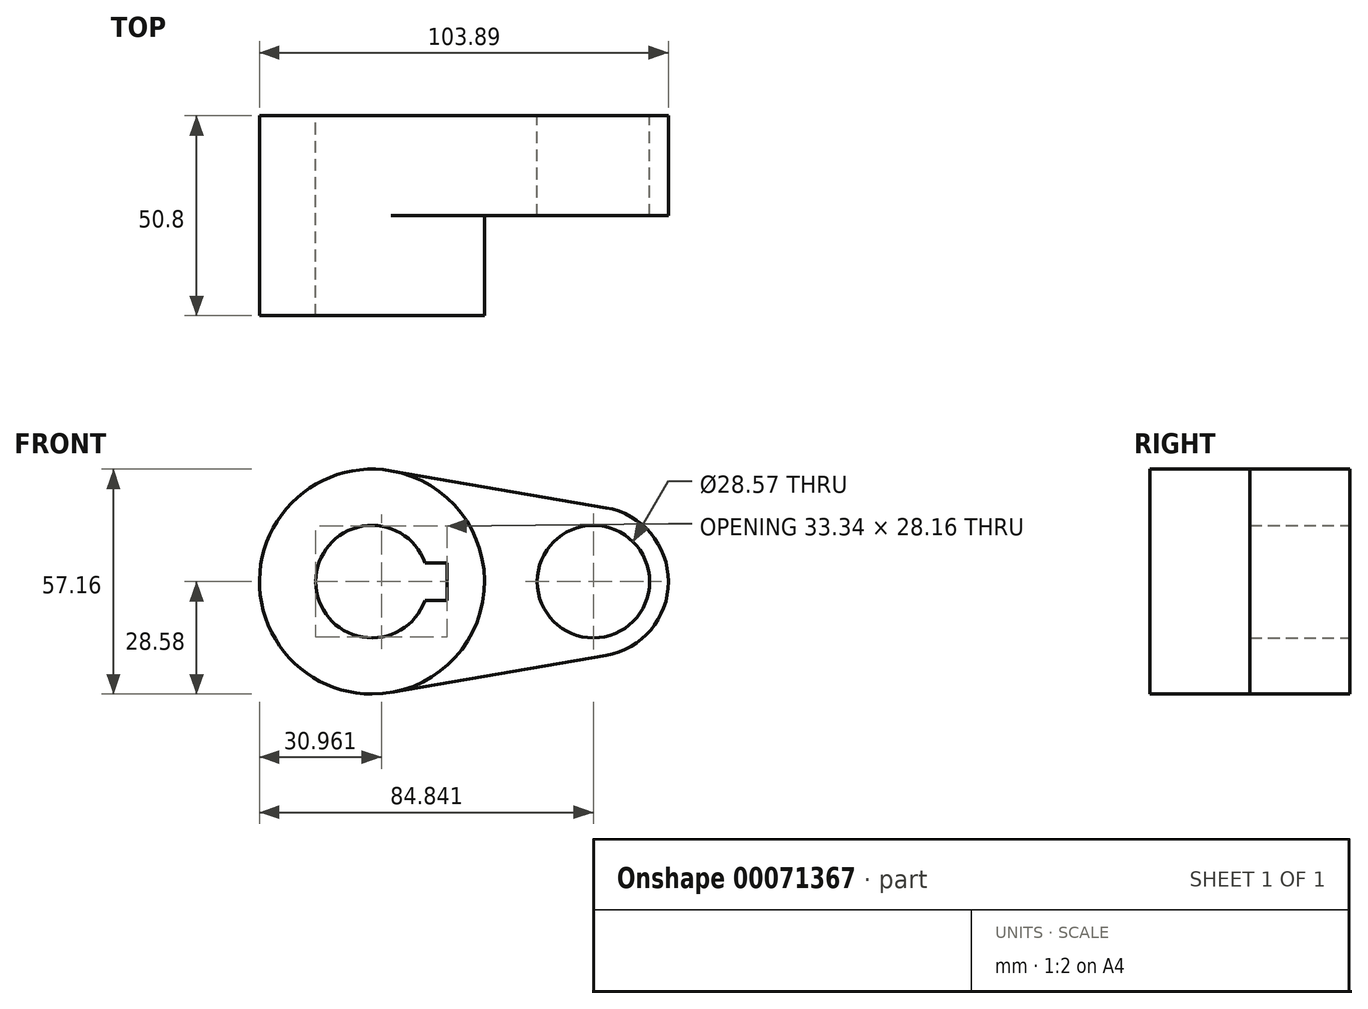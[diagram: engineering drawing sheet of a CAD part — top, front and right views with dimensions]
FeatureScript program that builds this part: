
annotation { "Feature Type Name" : "Feature", "Feature Type Description" : "" }
export const myFeature = defineFeature(function(context is Context, id is Id, definition is map)
    precondition{}
    {
        {
            var Q0;
            Q0=qCreatedBy(makeId("Front.planeOp"),FACE);
            var sketch = newSketch(context, id + "F0", { "sketchPlane" : qUnion([Q0])});
            skCircle(sketch, "E0", {"center": v(0, 0) * mm, "radius": 28.57 * mm});
            skCircle(sketch, "E1", {"center": v(56.26, 0) * mm, "radius": 19.05 * mm});
            skLineSegment(sketch, "E2", {"start": v(4.84, 28.16) * mm, "end": v(59.49, 18.78) * mm});
            skLineSegment(sketch, "E3", {"start": v(4.84, -28.16) * mm, "end": v(59.49, -18.78) * mm});
            skCircle(sketch, "E4", {"center": v(0, 0) * mm, "radius": 14.29 * mm});
            skCircle(sketch, "E5", {"center": v(56.26, 0) * mm, "radius": 14.29 * mm});
            skLineSegment(sketch, "E6.bottom", {"start": v(-19.05, 4.76) * mm, "end": v(19.05, 4.76) * mm});
            skLineSegment(sketch, "E6.top", {"start": v(-19.05, -4.76) * mm, "end": v(19.05, -4.76) * mm});
            skLineSegment(sketch, "E6.left", {"start": v(-19.05, 4.76) * mm, "end": v(-19.05, -4.76) * mm});
            skLineSegment(sketch, "E6.right", {"start": v(19.05, 4.76) * mm, "end": v(19.05, -4.76) * mm});
            skSolve(sketch);
        }
        {
            var Q0;
            {var subQ11=sQuery(id+"F0.wireOp",EDGE,"E6.left");Q0=makeQuery(id+"F0.imprint","IMPRINT",FACE,{"disambiguationData":[TD([[makeQuery(id+"F0.imprint","IMPRINT",EDGE,{"derivedFrom":subQ11}),-1.0]])]});}
            var Q1;
            {var subQ5=sQuery(id+"F0.wireOp",EDGE,"E6.left");Q1=makeQuery(id+"F0.imprint","IMPRINT",FACE,{"disambiguationData":[TD([[makeQuery(id+"F0.imprint","IMPRINT",EDGE,{"derivedFrom":subQ5}),1.0]])]});}
            var Q2;
            {var subQ0=sQuery(id+"F0.wireOp",EDGE,"E2");Q2=makeQuery(id+"F0.imprint","IMPRINT",FACE,{"disambiguationData":[TD([[makeQuery(id+"F0.imprint","IMPRINT",EDGE,{"derivedFrom":subQ0}),-1.0]])]});}
            var Q3;
            Q3=makeQuery(id+"F0.imprint","IMPRINT",FACE,{"disambiguationData":[TD([[makeQuery(id+"F0.imprint","IMPRINT",EDGE,{"derivedFrom":sQuery(id+"F0.wireOp",EDGE,"E5")}),-1.0]])]});
            extrude(context, id + "F1", {"entities" : qUnion([Q0, Q1, Q2, Q3]), "depth" : 25.4 * mm});
        }
        {
            var Q0;
            {var subQ11=sQuery(id+"F0.wireOp",EDGE,"E6.left");Q0=makeQuery(id+"F0.imprint","IMPRINT",FACE,{"disambiguationData":[TD([[makeQuery(id+"F0.imprint","IMPRINT",EDGE,{"derivedFrom":subQ11}),-1.0]])]});}
            var Q1;
            {var subQ5=sQuery(id+"F0.wireOp",EDGE,"E6.left");Q1=makeQuery(id+"F0.imprint","IMPRINT",FACE,{"disambiguationData":[TD([[makeQuery(id+"F0.imprint","IMPRINT",EDGE,{"derivedFrom":subQ5}),1.0]])]});}
            extrude(context, id + "F2", {"entities" : qUnion([Q0, Q1]), "operationType" : NewBodyOperationType.ADD, "depth" : 50.8 * mm});
        }
    });
